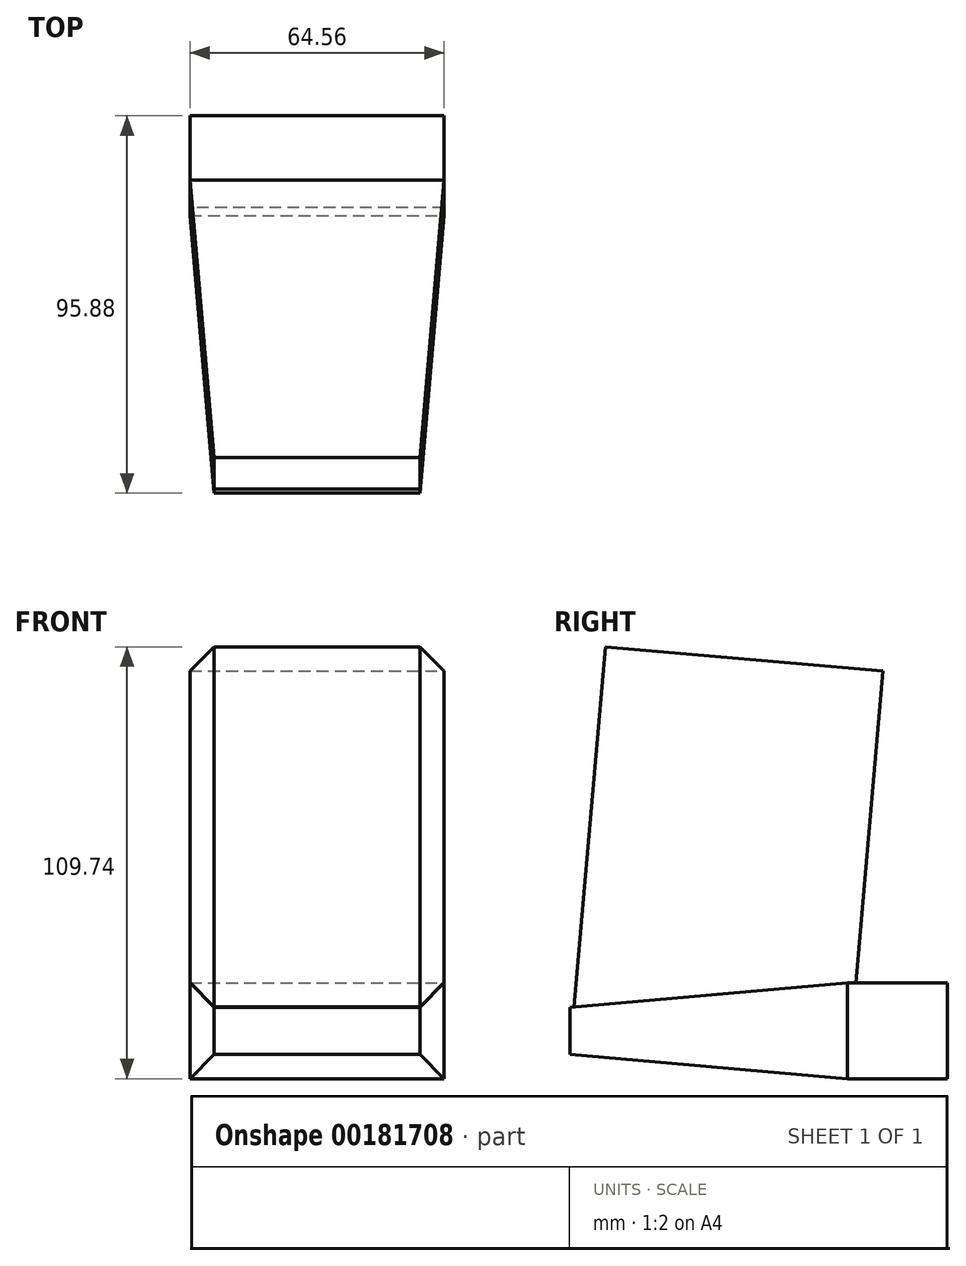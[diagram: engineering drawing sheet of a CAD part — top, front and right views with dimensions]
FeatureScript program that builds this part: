
annotation { "Feature Type Name" : "Feature", "Feature Type Description" : "" }
export const myFeature = defineFeature(function(context is Context, id is Id, definition is map)
    precondition{}
    {
        {
            var Q0;
            Q0=qCreatedBy(makeId("Front.planeOp"),FACE);
            var sketch = newSketch(context, id + "F0", { "sketchPlane" : qUnion([Q0])});
            skLineSegment(sketch, "E0.bottom", {"start": v(-46.31, 52.56) * mm, "end": v(18.25, 52.56) * mm});
            skLineSegment(sketch, "E0.top", {"start": v(-46.31, 28.23) * mm, "end": v(18.25, 28.23) * mm});
            skLineSegment(sketch, "E0.left", {"start": v(-46.31, 52.56) * mm, "end": v(-46.31, 28.23) * mm});
            skLineSegment(sketch, "E0.right", {"start": v(18.25, 52.56) * mm, "end": v(18.25, 28.23) * mm});
            skSolve(sketch);
        }
        {
            var Q0;
            Q0=makeQuery(id+"F0.imprint","IMPRINT",FACE,{"disambiguationData":[TD([[makeQuery(id+"F0.imprint","IMPRINT",EDGE,{"derivedFrom":sQuery(id+"F0.wireOp",EDGE,"E0.bottom")}),-1.0]])]});
            extrude(context, id + "F1", {"entities" : qUnion([Q0]), "depth" : 70.48 * mm, "hasDraft" : true, "draftAngle" : 5 * degree, "draftPullDirection" : true, "hasSecondDirection" : true, "secondDirectionOppositeDirection" : true, "secondDirectionDepth" : 25.4 * mm});
        }
        {
            var Q0;
            Q0=makeQuery(id+"F1.*.split.splitOp","SPLIT",FACE,{"derivedFrom":makeQuery(id+"F1.opExtrude","SWEPT_FACE",FACE,{"disambiguationData":[OSD([sQuery(id+"F0.wireOp",EDGE,"E0.top")])]})});
            extrude(context, id + "F2", {"entities" : qUnion([Q0]), "operationType" : NewBodyOperationType.ADD, "oppositeDirection" : true, "depth" : 103.97 * mm});
        }
    });
